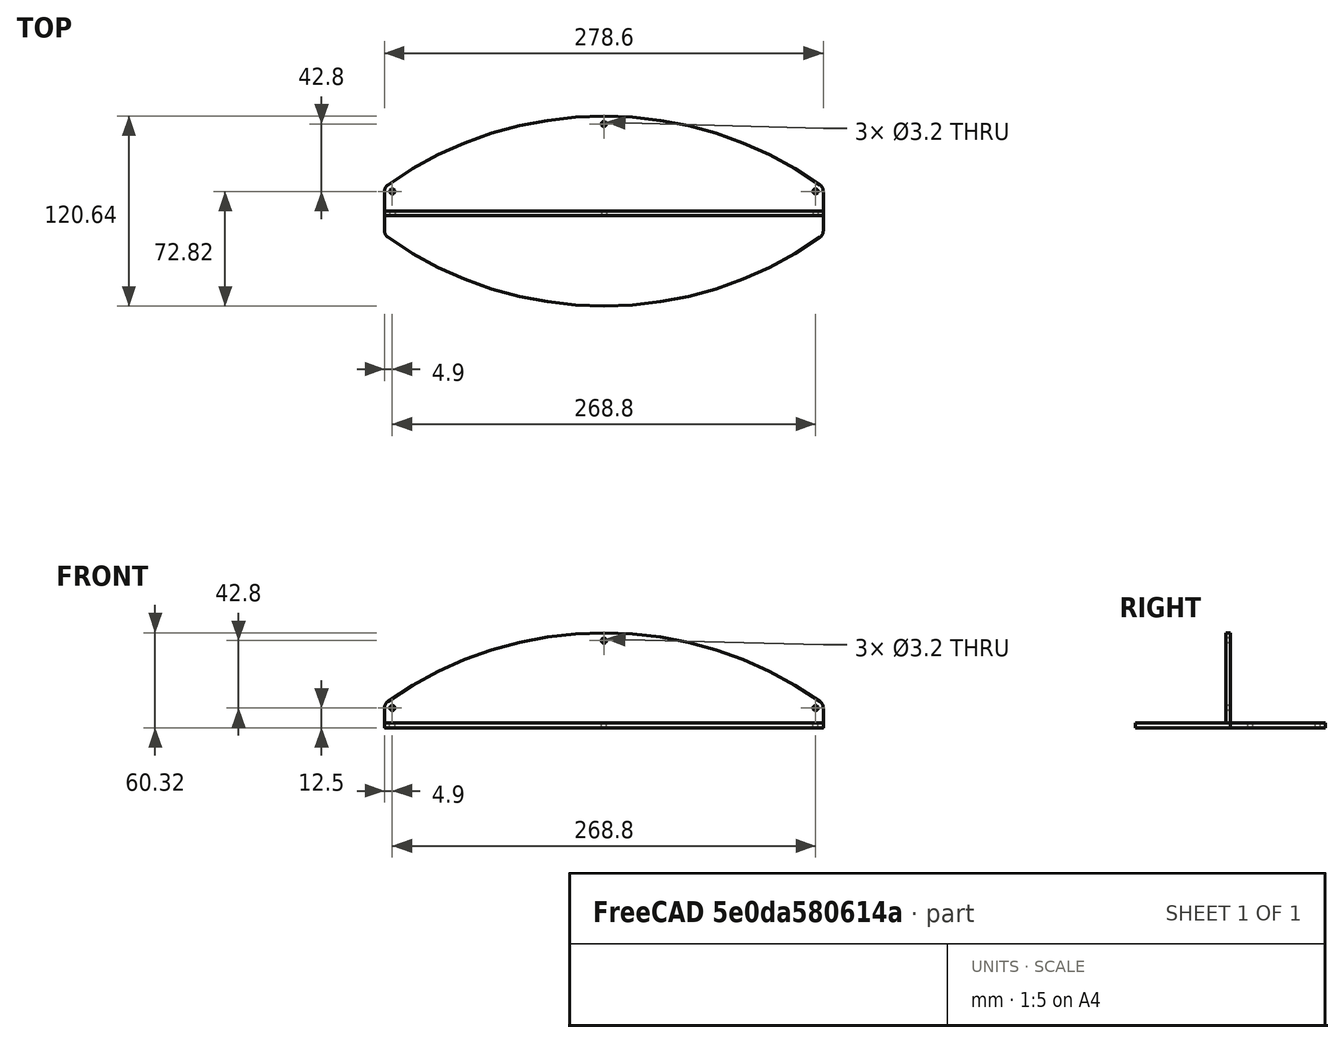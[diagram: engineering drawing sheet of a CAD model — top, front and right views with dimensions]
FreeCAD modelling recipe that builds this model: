
FCSTD DOCUMENT  (FreeCAD 0.19R24276 (Git))
Label: menorah_base
License: All rights reserved
LicenseURL: http://en.wikipedia.org/wiki/All_rights_reserved
objects: Part::Box×12, Part::Cylinder×10, Part::MultiFuse×8, Part::Cut×6, Part::Fillet×4
note: 40 computed .brp shape members not serialized (recipe doc carries the construction recipe); baked Part::Feature solids carry a one-line shape summary decoded from their .brp

FEATURE [Part::Cylinder] Cylinder
  Angle = 360
  AttacherType = Attacher::AttachEngine3D
  Height = 3
  Placement = pos=(0,0,0) rot=(1,0,0;1.5708rad)
  Radius = 237.321
FEATURE [Part::Box] Box  label="right cut"
  AttacherType = Attacher::AttachEngine3D
  Height = 400
  Length = 100
  Placement = pos=(139.3,-6,-205) rot=(0,0,1;0rad)
  Width = 10
FEATURE [Part::Box] Box001  label="left cut"
  AttacherType = Attacher::AttachEngine3D
  Height = 400
  Length = 100
  Placement = pos=(-139.3,3,-205) rot=(0,0,1;3.14159rad)
  Width = 10
FEATURE [Part::Box] Box002  label="bottom cut"
  AttacherType = Attacher::AttachEngine3D
  Height = 800
  Length = 800
  Placement = pos=(400,-7,177) rot=(0,1,0;3.14159rad)
  Width = 10
FEATURE [Part::MultiFuse] Fusion  label="left right bottom cuts"
  Shapes = -> [Box,Box001,Box002]
FEATURE [Part::Cut] Cut
  Base = -> Cylinder
  Placement = pos=(0,0,-190) rot=(0,0,1;0rad)
  Tool = -> Fusion
FEATURE [Part::Fillet] Fillet  label="vertical, no holes"
  Base = -> Cut
  Edges = 2 edges r=4.9: [Edge2,Edge4]
  Placement = pos=(0,0,0.5) rot=(0,0,1;0rad)
FEATURE [Part::Box] Box003  label="bottom cut001"
  AttacherType = Attacher::AttachEngine3D
  Height = 800
  Length = 800
  Placement = pos=(400,-7,177) rot=(0,1,0;3.14159rad)
  Width = 10
FEATURE [Part::Box] Box004  label="right cut001"
  AttacherType = Attacher::AttachEngine3D
  Height = 400
  Length = 100
  Placement = pos=(139.3,-6,-205) rot=(0,0,1;0rad)
  Width = 10
FEATURE [Part::Cylinder] Cylinder001
  Angle = 360
  AttacherType = Attacher::AttachEngine3D
  Height = 3
  Placement = pos=(0,0,0) rot=(1,0,0;1.5708rad)
  Radius = 237.321
FEATURE [Part::Box] Box005  label="left cut001"
  AttacherType = Attacher::AttachEngine3D
  Height = 400
  Length = 100
  Placement = pos=(-139.3,3,-205) rot=(0,0,1;3.14159rad)
  Width = 10
FEATURE [Part::MultiFuse] Fusion001  label="left right bottom cuts001"
  Shapes = -> [Box004,Box005,Box003]
FEATURE [Part::Cut] Cut001
  Base = -> Cylinder001
  Placement = pos=(0,0,-190) rot=(0,0,1;0rad)
  Tool = -> Fusion001
FEATURE [Part::Fillet] Fillet001  label="horizontal"
  Base = -> Cut001
  Edges = 2 edges r=4.9: [Edge2,Edge4]
  Placement = pos=(0,-13,-9.5) rot=(1,0,0;1.5708rad)
FEATURE [Part::Cylinder] Cylinder002  label="ctr hole"
  Angle = 360
  AttacherType = Attacher::AttachEngine3D
  Height = 10
  Placement = pos=(0,0,42.8) rot=(1,0,0;1.5708rad)
  Radius = 1.6
FEATURE [Part::Cylinder] Cylinder003  label="left hole"
  Angle = 360
  AttacherType = Attacher::AttachEngine3D
  Height = 10
  Placement = pos=(-134.4,4,0) rot=(1,0,0;1.5708rad)
  Radius = 1.6
FEATURE [Part::Cylinder] Cylinder004  label="right hole"
  Angle = 360
  AttacherType = Attacher::AttachEngine3D
  Height = 10
  Placement = pos=(134.4,4,0) rot=(1,0,0;1.5708rad)
  Radius = 1.6
FEATURE [Part::MultiFuse] Fusion002  label="screw holes"
  Shapes = -> [Cylinder004,Cylinder002,Cylinder003]
FEATURE [Part::Cut] Cut002  label="vertical"
  Base = -> Fillet
  Tool = -> Fusion002
FEATURE [Part::MultiFuse] Fusion003  label="bent version"
  Placement = pos=(0,-1.6,0) rot=(0,0,1;0rad)
  Shapes = -> [Fillet001,Cut002]
FEATURE [Part::Box] Box006  label="bottom cut002"
  AttacherType = Attacher::AttachEngine3D
  Height = 800
  Length = 800
  Placement = pos=(400,-7,177) rot=(0,1,0;3.14159rad)
  Width = 10
FEATURE [Part::Cylinder] Cylinder005  label="right hole001"
  Angle = 360
  AttacherType = Attacher::AttachEngine3D
  Height = 10
  Placement = pos=(134.4,4,0) rot=(1,0,0;1.5708rad)
  Radius = 1.6
FEATURE [Part::Box] Box007  label="left cut002"
  AttacherType = Attacher::AttachEngine3D
  Height = 400
  Length = 100
  Placement = pos=(-139.3,3,-205) rot=(0,0,1;3.14159rad)
  Width = 10
FEATURE [Part::Cylinder] Cylinder006  label="left hole001"
  Angle = 360
  AttacherType = Attacher::AttachEngine3D
  Height = 10
  Placement = pos=(-134.4,4,0) rot=(1,0,0;1.5708rad)
  Radius = 1.6
FEATURE [Part::Box] Box008  label="left cut003"
  AttacherType = Attacher::AttachEngine3D
  Height = 400
  Length = 100
  Placement = pos=(-139.3,3,-205) rot=(0,0,1;3.14159rad)
  Width = 10
FEATURE [Part::Cylinder] Cylinder007
  Angle = 360
  AttacherType = Attacher::AttachEngine3D
  Height = 3
  Placement = pos=(0,0,0) rot=(1,0,0;1.5708rad)
  Radius = 237.321
FEATURE [Part::Box] Box009  label="bottom cut003"
  AttacherType = Attacher::AttachEngine3D
  Height = 800
  Length = 800
  Placement = pos=(400,-7,177) rot=(0,1,0;3.14159rad)
  Width = 10
FEATURE [Part::Cylinder] Cylinder008  label="ctr hole001"
  Angle = 360
  AttacherType = Attacher::AttachEngine3D
  Height = 10
  Placement = pos=(0,0,42.8) rot=(1,0,0;1.5708rad)
  Radius = 1.6
FEATURE [Part::MultiFuse] Fusion005  label="screw holes001"
  Shapes = -> [Cylinder005,Cylinder008,Cylinder006]
FEATURE [Part::Cylinder] Cylinder009
  Angle = 360
  AttacherType = Attacher::AttachEngine3D
  Height = 3
  Placement = pos=(0,0,0) rot=(1,0,0;1.5708rad)
  Radius = 237.321
FEATURE [Part::Box] Box010  label="right cut002"
  AttacherType = Attacher::AttachEngine3D
  Height = 400
  Length = 100
  Placement = pos=(139.3,-6,-205) rot=(0,0,1;0rad)
  Width = 10
FEATURE [Part::MultiFuse] Fusion006  label="left right bottom cuts003"
  Shapes = -> [Box010,Box007,Box009]
FEATURE [Part::Cut] Cut005
  Base = -> Cylinder009
  Placement = pos=(0,0,-190) rot=(0,0,1;0rad)
  Tool = -> Fusion006
FEATURE [Part::Fillet] Fillet002  label="horizontal001"
  Base = -> Cut005
  Edges = 2 edges r=4.9: [Edge2,Edge4]
  Placement = pos=(0,-13,-9.5) rot=(1,0,0;1.5708rad)
FEATURE [Part::Box] Box011  label="right cut003"
  AttacherType = Attacher::AttachEngine3D
  Height = 400
  Length = 100
  Placement = pos=(139.3,-6,-205) rot=(0,0,1;0rad)
  Width = 10
FEATURE [Part::MultiFuse] Fusion004  label="left right bottom cuts002"
  Shapes = -> [Box011,Box008,Box006]
FEATURE [Part::Cut] Cut003
  Base = -> Cylinder007
  Placement = pos=(0,0,-190) rot=(0,0,1;0rad)
  Tool = -> Fusion004
FEATURE [Part::Fillet] Fillet003  label="vertical, no holes001"
  Base = -> Cut003
  Edges = 2 edges r=4.9: [Edge2,Edge4]
  Placement = pos=(0,0,0.5) rot=(0,0,1;0rad)
FEATURE [Part::Cut] Cut004  label="vertical001"
  Base = -> Fillet003
  Placement = pos=(0,12.5,-12.5) rot=(1,0,0;4.71239rad)
  Tool = -> Fusion005
FEATURE [Part::MultiFuse] Fusion007  label="flat"
  Placement = pos=(0,-1.6,0) rot=(0,0,1;0rad)
  Shapes = -> [Fillet002,Cut004]
